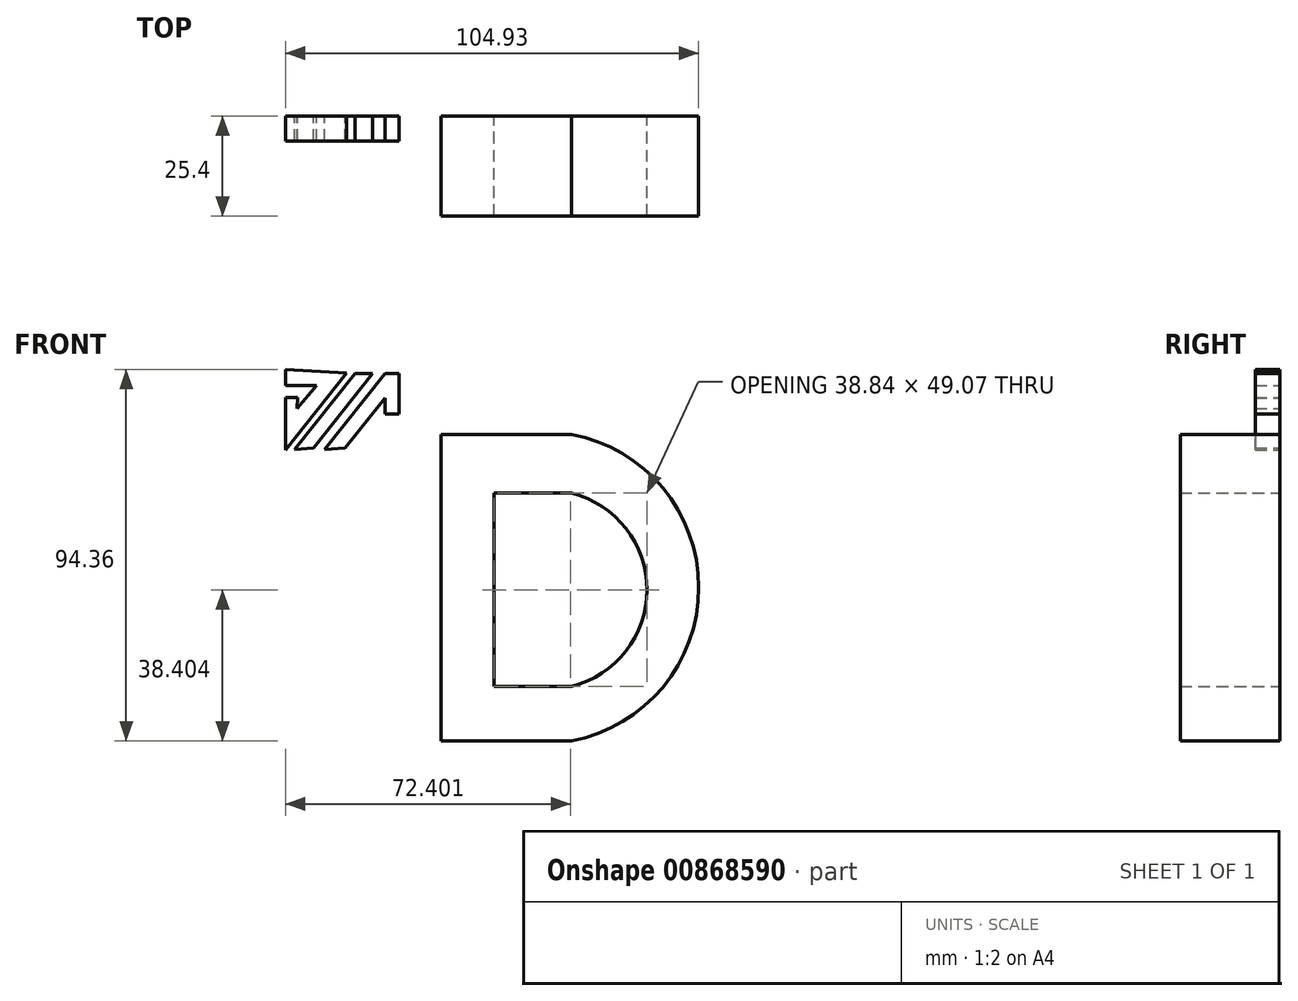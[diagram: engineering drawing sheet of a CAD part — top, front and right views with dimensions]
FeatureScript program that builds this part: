
annotation { "Feature Type Name" : "Feature", "Feature Type Description" : "" }
export const myFeature = defineFeature(function(context is Context, id is Id, definition is map)
    precondition{}
    {
        {
            var Q0;
            Q0=qCreatedBy(makeId("Front.planeOp"),FACE);
            var sketch = newSketch(context, id + "F0", { "sketchPlane" : qUnion([Q0])});
            skLineSegment(sketch, "E0.bottom", {"start": v(-33.16, 35.12) * mm, "end": v(0, 35.12) * mm});
            skLineSegment(sketch, "E0.top", {"start": v(-33.16, -42.76) * mm, "end": v(0, -42.76) * mm});
            skArc(sketch, "E1", {"start": v(0, -42.76) * mm, "mid": v(32.3, -3.82) * mm, "end": v(0, 35.12) * mm});
            skLineSegment(sketch, "E2.bottom", {"start": v(-19.65, 20.18) * mm, "end": v(0, 20.18) * mm});
            skLineSegment(sketch, "E2.top", {"start": v(-19.65, -28.9) * mm, "end": v(0, -28.9) * mm});
            skLineSegment(sketch, "E2.left", {"start": v(-19.65, 20.18) * mm, "end": v(-19.65, -28.9) * mm});
            skArc(sketch, "E3", {"start": v(0, -28.9) * mm, "mid": v(19.19, -4.36) * mm, "end": v(0, 20.18) * mm});
            skLineSegment(sketch, "E4", {"start": v(-33.16, 35.12) * mm, "end": v(-33.16, -42.76) * mm});
            skSolve(sketch);
        }
        {
            var Q0;
            Q0=makeQuery(id+"F0.imprint","IMPRINT",FACE,{"disambiguationData":[TD([[makeQuery(id+"F0.imprint","IMPRINT",EDGE,{"derivedFrom":sQuery(id+"F0.wireOp",EDGE,"E0.bottom")}),-1.0]])]});
            extrude(context, id + "F1", {"entities" : qUnion([Q0]), "depth" : 25.4 * mm, "offsetDistance" : 25.4 * mm});
        }
        {
            var Q0;
            Q0=qCreatedBy(makeId("Front.planeOp"),FACE);
            var sketch = newSketch(context, id + "F2", { "sketchPlane" : qUnion([Q0])});
            skLineSegment(sketch, "E5", {"start": v(-72.63, 51.6) * mm, "end": v(-72.63, 47.56) * mm});
            skLineSegment(sketch, "E6", {"start": v(-72.63, 31.2) * mm, "end": v(-57.15, 50.76) * mm});
            skLineSegment(sketch, "E7", {"start": v(-57.15, 50.76) * mm, "end": v(-72.63, 51.6) * mm});
            skLineSegment(sketch, "E8", {"start": v(-72.63, 47.56) * mm, "end": v(-69.43, 47.56) * mm});
            skLineSegment(sketch, "E9", {"start": v(-69.6, 44.46) * mm, "end": v(-69.74, 41.75) * mm});
            skLineSegment(sketch, "E10", {"start": v(-69.74, 41.75) * mm, "end": v(-64.8, 47.56) * mm});
            skLineSegment(sketch, "E11", {"start": v(-64.8, 47.56) * mm, "end": v(-69.43, 47.56) * mm});
            skLineSegment(sketch, "E12", {"start": v(-72.63, 44.46) * mm, "end": v(-69.43, 44.46) * mm});
            skLineSegment(sketch, "E13.trimOffspring", {"start": v(-72.63, 44.46) * mm, "end": v(-72.63, 31.2) * mm});
            skLineSegment(sketch, "E14", {"start": v(-70.36, 31.25) * mm, "end": v(-55.04, 50.61) * mm});
            skLineSegment(sketch, "E15", {"start": v(-55.04, 50.61) * mm, "end": v(-50.56, 50.61) * mm});
            skLineSegment(sketch, "E16", {"start": v(-50.56, 50.61) * mm, "end": v(-65.58, 31.63) * mm});
            skLineSegment(sketch, "E17", {"start": v(-65.58, 31.63) * mm, "end": v(-70.36, 31.25) * mm});
            skLineSegment(sketch, "E18", {"start": v(-62.7, 31.25) * mm, "end": v(-47.38, 50.61) * mm});
            skPoint(sketch, "E18.startSnap0", {"position": v(-62.7, 40.93) * mm});
            skLineSegment(sketch, "E19", {"start": v(-47.38, 50.61) * mm, "end": v(-43.85, 50.61) * mm});
            skLineSegment(sketch, "E20", {"start": v(-43.85, 50.61) * mm, "end": v(-43.85, 40.27) * mm});
            skLineSegment(sketch, "E21", {"start": v(-43.85, 40.27) * mm, "end": v(-47.38, 40.27) * mm});
            skLineSegment(sketch, "E22", {"start": v(-47.38, 40.27) * mm, "end": v(-47.38, 44.4) * mm});
            skLineSegment(sketch, "E23", {"start": v(-47.38, 44.4) * mm, "end": v(-57.5, 31.63) * mm});
            skLineSegment(sketch, "E24", {"start": v(-57.5, 31.63) * mm, "end": v(-62.7, 31.25) * mm});
            skSolve(sketch);
        }
        {
            var Q0;
            Q0 = qSketchRegion(id + "F2", true);
            extrude(context, id + "F3", {"entities" : qUnion([Q0]), "depth" : 6.35 * mm, "offsetDistance" : 25.4 * mm});
        }
    });
